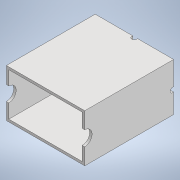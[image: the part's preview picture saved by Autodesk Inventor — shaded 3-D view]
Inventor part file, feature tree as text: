
AUTODESK INVENTOR PART (.ipt)
format: ipt  version: 2022 (Build 260153000, 153)  size: 252,928 bytes
history: native  units: in
note: dims shown in document units (in); Inventor stores cm internally (conversion verified against a paired STEP export)
features: extrude x9, sketch x8, reference x8, other x6, projected_geometry x2, plane x1, fillet x1
ambient origin geometry x8: Origin, YZ Plane, XZ Plane, XY Plane, X Axis, Y Axis, Z Axis, Center Point
bodies: Solid1 (feature_tree)
feature tree (35):
  extrude  "Extrusion1"  Depth=0.0039in
  extrude  "Extrusion4"  Depth=0.0787in
  extrude  "Extrusion5"  Depth=0.0039in
  extrude  "Extrusion6"  Depth=0.1969in
  sketch  "Sketch7"  dims[d12=0.4724in d13=0.0in d23=6.6535in d24=0.0in]
  plane  "Work Plane2"
  extrude  "Extrusion7"  Depth=6.6535in TaperAngle=0.0deg
  extrude  "Extrusion8"  Depth=6.2992in TaperAngle=0.0deg
  extrude  "Extrusion9"  Depth=0.3937in TaperAngle=0.0deg
  extrude  "Extrusion10"  TaperAngle=0.0deg  [1 undecoded]
  fillet  "Fillet2"  Radius=0.2087in
  extrude  "Extrusion13"  Depth=6.2992in
  sketch  "Sketch1"  dims[d0=0.0039in d1=0.0039in]
  reference  "Reference1"
  reference  "Reference2"
  sketch  "Sketch4"  dims[d2=0.0039in d6=0.0787in]
  reference  "Reference6"
  sketch  "Sketch5"  dims[d8=0.0039in d9=0.0039in]
  projected_geometry  "Projected Loop1"
  sketch  "Sketch6"  dims[d10=0.0039in d11=0.1969in]
  projected_geometry  "Projected Loop2"
  sketch  "Sketch8"  dims[d26=0.1969in d27=6.2992in d28=0.0in]
  reference  "Reference9"
  sketch  "Sketch10"  dims[d29=3.937in d30=0.0in d32=0.3937in d33=0.0in]
  reference  "Reference24"
  reference  "Reference25"
  reference  "Reference26"
  reference  "Reference27"
  sketch  "Sketch13"  dims[d34=0.3937in d35=0.0in d36=0.0in d37=0.2087in d38=0.2953in d39=0.5906in d40=1.5748in d42=0.5906in d43=0.3937in d45=0.3937in d47=1.7717in d48=0.0in d49=1.5748in d51=0.0in d52=0.0in d65=0.3937in d66=0.1969in d71=0.3937in d72=0.0039in d73=0.0039in d74=0.0051in d75=0.0039in d77=1.5748in d78=3.1496in d79=6.2992in d80=0.0in d31=0.0197in]
  other  "Linear Rail Assembly.iam"
  other  "backboard:1"
  other  "endcap insert_MIR:1"
  other  "SyringeHolder:1"
  other  "Linear Rail Frame Bracket_MIR:1"
  other  "Linear Rail motor:1"
note: 1 required parameter value undecoded (feature->parameter linkage not recoverable at this tier; creation-order binding heuristic only, values carry confidence <= 0.55)
